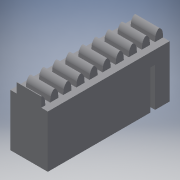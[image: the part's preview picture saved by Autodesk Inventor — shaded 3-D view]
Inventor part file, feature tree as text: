
AUTODESK INVENTOR PART (.ipt)
format: ipt  version: 2016 (Build 200138000, 138)  size: 361,472 bytes
history: native  units: in
note: dims shown in document units (in); Inventor stores cm internally (conversion verified against a paired STEP export)
features: extrude x9, sketch x9, projected_geometry x4
ambient origin geometry x8: Origin, YZ Plane, XZ Plane, XY Plane, X Axis, Y Axis, Z Axis, Center Point
bodies: Body1 (feature_tree)
feature tree (22):
  extrude  "Extrusion2"  Depth=0.435in
  sketch  "Sketch3"  dims[d6=0.385in d7=0.0in d9=0.092in]
  extrude  "Extrusion4"  Depth=0.385in
  extrude  "Extrusion6"  Depth=0.075in
  extrude  "Extrusion7"  Depth=0.05in
  extrude  "Extrusion8"  Depth=0.1in TaperAngle=0.0deg
  extrude  "Extrusion9"  Depth=0.385in TaperAngle=0.0deg
  extrude  "Extrusion10"  Depth=0.5814in
  extrude  "Extrusion11"  Depth=0.25in TaperAngle=0.0deg
  extrude  "Extrusion12"  Depth=0.385in TaperAngle=0.0deg
  sketch  "Sketch2"  dims[d4=2.5in d5=0.435in]
  sketch  "Sketch4"  dims[d28=0.075in d29=0.075in]
  sketch  "Sketch5"  dims[d31=0.1in d32=0.05in]
  projected_geometry  "Projected Loop1"
  projected_geometry  "Projected Loop2"
  projected_geometry  "Projected Loop3"
  sketch  "Sketch6"  dims[d33=0.4in d34=0.0in d58=0.1in d59=0.0in]
  sketch  "Sketch7"  dims[d60=0.1in d61=0.385in d62=0.0in]
  sketch  "Sketch8"  dims[d63=0.5814in d64=0.5814in]
  sketch  "Sketch9"  dims[d72=7.4803in d74=0.1342in d75=0.3937in d77=1.0in d79=0.25in d80=0.0in]
  projected_geometry  "Projected Loop4"
  sketch  "Sketch10"  dims[d81=0.05in d82=0.385in d83=0.0in d84=0.15in d85=0.05in d86=0.4in d87=0.385in d88=0.0in d89=0.385in d90=0.0in d91=1.0in d92=0.0in]
